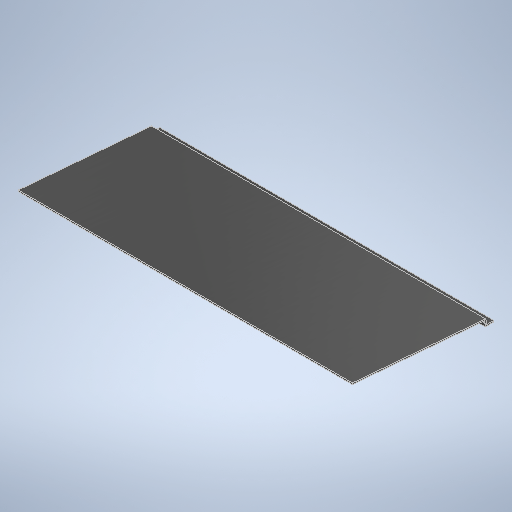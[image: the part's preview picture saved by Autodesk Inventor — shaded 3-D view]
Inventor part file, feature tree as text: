
AUTODESK INVENTOR PART (.ipt)
format: ipt  version: 2025.1 (Build 291241020, 241B)  size: 262,144 bytes
history: native  units: in
note: dims shown in document units (in); Inventor stores cm internally (conversion verified against a paired STEP export)
features: extrude x1, sketch x1
ambient origin geometry x8: Origin, YZ Plane, XZ Plane, XY Plane, X Axis, Y Axis, Z Axis, Center Point
bodies: Body1 (feature_tree)
feature tree (2):
  extrude  "Extrusion2"  Depth=0.125in
  sketch  "Sketch1"  dims[d0=23.408in d1=0.125in d2=0.265in d7=0.125in d8=0.237in d9=1.1431in d10=0.125in d11=0.7449in d12=0.125in d13=12.09in d16=0.125in d18=0.125in d20=12.0907in d21=0.3425in d22=0.125in d23=0.125in d24=0.1549in d25=0.661in d26=30.45in d27=0.0in]
